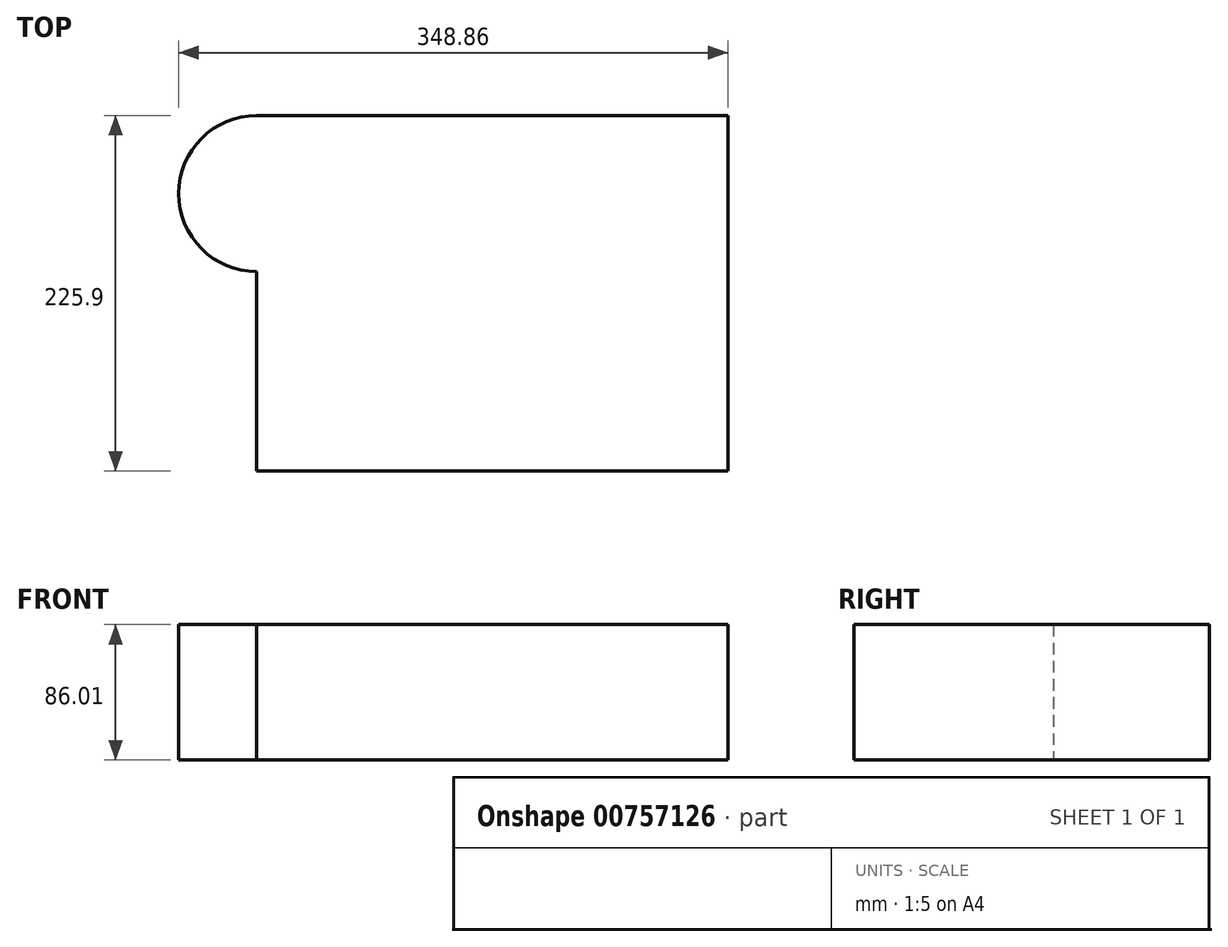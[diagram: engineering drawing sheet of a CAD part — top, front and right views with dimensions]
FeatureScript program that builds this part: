
annotation { "Feature Type Name" : "Feature", "Feature Type Description" : "" }
export const myFeature = defineFeature(function(context is Context, id is Id, definition is map)
    precondition{}
    {
        {
            var Q0;
            Q0=qCreatedBy(makeId("Top.planeOp"),FACE);
            var sketch = newSketch(context, id + "F0", { "sketchPlane" : qUnion([Q0])});
            skLineSegment(sketch, "E0.bottom", {"start": v(0, 0) * mm, "end": v(0, 0) * mm});
            skLineSegment(sketch, "E0.top", {"start": v(0, 0) * mm, "end": v(0, 0) * mm});
            skLineSegment(sketch, "E0.left", {"start": v(0, 0) * mm, "end": v(0, 0) * mm});
            skLineSegment(sketch, "E0.right", {"start": v(0, 0) * mm, "end": v(0, 0) * mm});
            skLineSegment(sketch, "E1.bottom", {"start": v(149.63, 112.95) * mm, "end": v(-149.63, 112.95) * mm});
            skLineSegment(sketch, "E1.top", {"start": v(149.63, -112.95) * mm, "end": v(-149.63, -112.95) * mm});
            skLineSegment(sketch, "E1.left", {"start": v(149.63, 112.95) * mm, "end": v(149.63, -112.95) * mm});
            skLineSegment(sketch, "E1.right", {"start": v(-149.63, 112.95) * mm, "end": v(-149.63, -112.95) * mm});
            skPoint(sketch, "E1.middle", {"position": v(0, 0) * mm});
            skArc(sketch, "E2", {"start": v(149.63, 112.95) * mm, "mid": v(206.1, 56.48) * mm, "end": v(149.63, 0) * mm});
            skArc(sketch, "E3", {"start": v(-149.63, 112.95) * mm, "mid": v(-199.23, 63.35) * mm, "end": v(-149.63, 13.75) * mm});
            skSolve(sketch);
        }
        {
            var Q0;
            {var subQ4=sQuery(id+"F0.wireOp",EDGE,"E1.bottom");Q0=makeQuery(id+"F0.imprint","IMPRINT",FACE,{"disambiguationData":[TD([[makeQuery(id+"F0.imprint","IMPRINT",EDGE,{"derivedFrom":subQ4}),1.0]])]});}
            var Q1;
            {var subQ0=sQuery(id+"F0.wireOp",EDGE,"E3");Q1=makeQuery(id+"F0.imprint","IMPRINT",FACE,{"disambiguationData":[TD([[makeQuery(id+"F0.imprint","IMPRINT",EDGE,{"derivedFrom":subQ0}),1.0]])]});}
            var Q2;
            {var subQ0=sQuery(id+"F0.wireOp",EDGE,"E2");Q2=makeQuery(id+"F0.imprint","IMPRINT",FACE,{"disambiguationData":[TD([[makeQuery(id+"F0.imprint","IMPRINT",EDGE,{"derivedFrom":subQ0}),-1.0]])]});}
            extrude(context, id + "F1", {"entities" : qUnion([Q0, Q1, Q2]), "depth" : 86 * mm, "offsetDistance" : 25.4 * mm});
        }
    });
